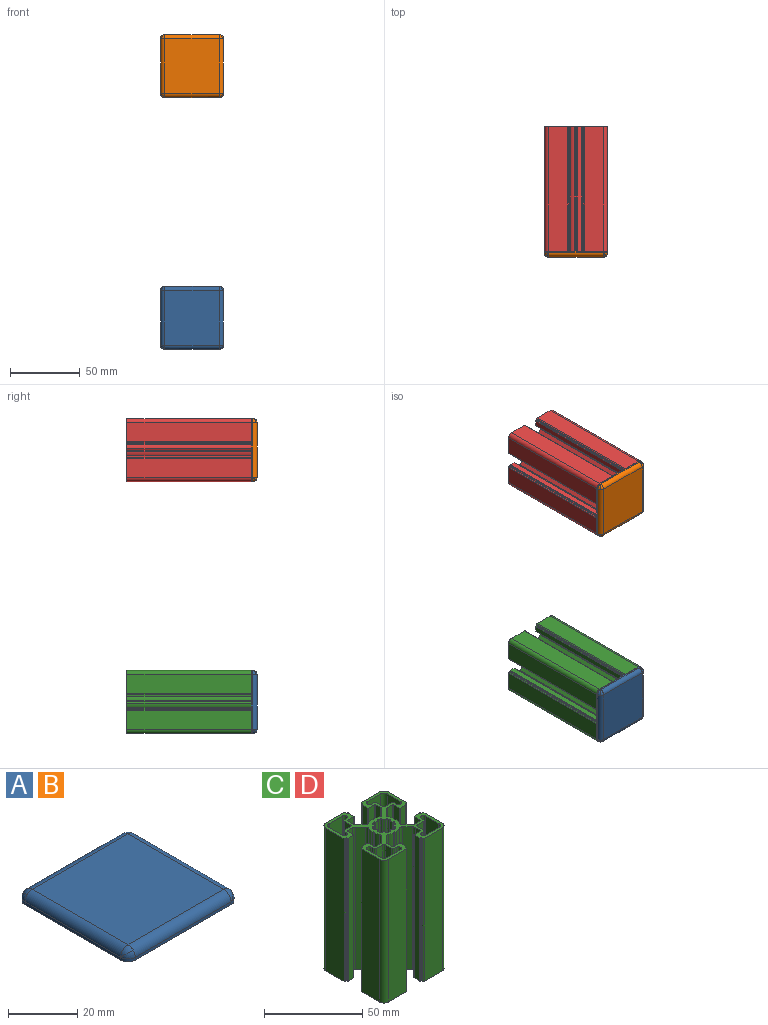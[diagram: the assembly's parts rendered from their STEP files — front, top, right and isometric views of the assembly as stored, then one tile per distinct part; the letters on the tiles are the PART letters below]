
ASSEMBLY  parts=4 mates=3
PART A: 22 faces, bbox 45x45x5.1 mm
  f0: sphere r=3mm, area 7.1mm2, adj f11,f12,f19
  f1: sphere r=3mm, area 7.1mm2, adj f9,f10,f17
  f2: sphere r=3mm, area 7.1mm2, adj f7,f8,f15
  f3: sphere r=3mm, area 7.1mm2, adj f5,f6,f12
  f4: plane 39x39mm, normal (0,0,1), area 1521mm2, adj f6,f8,f10,f12
  f5: sphere r=3mm, area 7.1mm2, adj f3,f12,f13
  f6: cylinder r=3mm len=39mm, axis (-1,0,0), area 183.8mm2, adj f3,f4,f7,f14
  f7: sphere r=3mm, area 7.1mm2, adj f2,f6,f8
  f8: cylinder r=3mm len=39mm, axis (0,-1,0), area 183.8mm2, adj f2,f4,f7,f9,f16
  f9: sphere r=3mm, area 7.1mm2, adj f1,f8,f10
  f10: cylinder r=3mm len=39mm, axis (1,0,0), area 183.8mm2, adj f1,f4,f9,f11,f18
  f11: sphere r=3mm, area 7.1mm2, adj f0,f10,f12
  f12: cylinder r=3mm len=39mm, axis (0,1,0), area 183.8mm2, adj f0,f3,f4,f5,f11,f20
  f13: cylinder r=3mm len=3mm, axis (0,0,-1), area 4.7mm2, adj f5,f14,f20,f21
  f14: plane 39x1mm, normal (0,1,0), area 39mm2, adj f6,f13,f15,f21
  f15: cylinder r=3mm len=3mm, axis (0,0,-1), area 4.7mm2, adj f2,f14,f16,f21
  f16: plane 39x1mm, normal (-1,0,0), area 39mm2, adj f8,f15,f17,f21
  f17: cylinder r=3mm len=3mm, axis (0,0,-1), area 4.7mm2, adj f1,f16,f18,f21
  f18: plane 39x1mm, normal (0,-1,0), area 39mm2, adj f10,f17,f19,f21
  f19: cylinder r=3mm len=3mm, axis (0,0,-1), area 4.7mm2, adj f0,f18,f20,f21
  f20: plane 39x1mm, normal (1,0,0), area 39mm2, adj f12,f13,f19,f21
  f21: plane 45x45mm, normal (0,0,-1), area 2017.3mm2, adj f13,f14,f15,f16,f17,f18,f19,f20
PART B: same geometry as A
PART C: 246 faces, bbox 45x45x89 mm
  f0: cylinder r=1.5mm len=89mm, axis (0,0,1), area 419.4mm2, adj f155,f156,f230,f231
  f1: cylinder r=1.5mm len=89mm, axis (0,0,1), area 419.4mm2, adj f155,f156,f212,f222
  f2: cylinder r=0.5mm len=89mm, axis (0,0,1), area 75.7mm2, adj f155,f156,f187,f188
  f3: cylinder r=0.5mm len=89mm, axis (0,0,1), area 75.7mm2, adj f155,f156,f182,f183
  f4: cylinder r=5mm len=89mm, axis (0,0,1), area 158.9mm2, adj f155,f156,f181,f182
  f5: cylinder r=0.5mm len=89mm, axis (0,0,1), area 75.7mm2, adj f155,f156,f180,f181
  f6: cylinder r=0.5mm len=89mm, axis (0,0,1), area 75.7mm2, adj f155,f156,f175,f176
  f7: cylinder r=0.2mm len=89mm, axis (0,0,1), area 11.2mm2, adj f153,f154,f155,f156
  f8: cylinder r=1.94mm len=89mm, axis (0,0,1), area 216.4mm2, adj f87,f88,f155,f156
  f9: cylinder r=1.94mm len=89mm, axis (0,0,1), area 216.4mm2, adj f79,f80,f155,f156
  f10: cylinder r=0.2mm len=89mm, axis (0,0,1), area 11.2mm2, adj f13,f14,f155,f156
  f11: cylinder r=0.2mm len=89mm, axis (0,0,1), area 4.2mm2, adj f12,f154,f155,f156
  f12: cylinder r=0.2mm len=89mm, axis (0,0,1), area 4.2mm2, adj f11,f13,f155,f156
  f13: plane 89x0.75mm, normal (0.86,0.5,0), area 76.8mm2, adj f10,f12,f155,f156
  f14: cylinder r=8mm len=89mm, axis (0,0,1), area 251.7mm2, adj f10,f15,f155,f156
  f15: cylinder r=1.94mm len=89mm, axis (0,0,1), area 216.4mm2, adj f14,f16,f155,f156
  f16: plane 89x3.57mm, normal (0.71,0.71,0), area 448.9mm2, adj f15,f17,f155,f156
  f17: cylinder r=1.94mm len=89mm, axis (0,0,1), area 135.9mm2, adj f16,f18,f155,f156
  f18: plane 89x3.81mm, normal (0,1,0), area 339.3mm2, adj f17,f19,f155,f156
  f19: cylinder r=0.2mm len=89mm, axis (0,0,1), area 28mm2, adj f18,f20,f155,f156
  f20: plane 89x4.59mm, normal (-1,0,0), area 408.9mm2, adj f19,f21,f155,f156
  f21: cylinder r=0.2mm len=89mm, axis (0,0,1), area 28mm2, adj f20,f22,f155,f156
  f22: plane 89x4mm, normal (0,1,0), area 356.2mm2, adj f21,f23,f155,f156
  f23: cylinder r=0.3mm len=89mm, axis (0,0,1), area 41.9mm2, adj f22,f24,f155,f156
  f24: plane 89x0.2mm, normal (1,0,0), area 17.8mm2, adj f23,f25,f155,f156
  f25: cylinder r=0.3mm len=89mm, axis (0,0,1), area 41.9mm2, adj f24,f26,f155,f156
  f26: plane 89x0.68mm, normal (0,1,0), area 60.6mm2, adj f25,f27,f155,f156
  f27: cylinder r=0.5mm len=89mm, axis (0,0,1), area 69.9mm2, adj f26,f28,f155,f156
  f28: plane 89x13.2mm, normal (1,0,0), area 1174.8mm2, adj f27,f29,f155,f156
  f29: cylinder r=3mm len=89mm, axis (0,0,1), area 419.4mm2, adj f28,f30,f155,f156
  f30: plane 89x13.12mm, normal (0,-1,0), area 1168.1mm2, adj f29,f31,f155,f156
  f31: cylinder r=0.5mm len=89mm, axis (0,0,1), area 69.9mm2, adj f30,f32,f155,f156
  f32: plane 89x0.7mm, normal (-1,0,0), area 62.3mm2, adj f31,f33,f155,f156
  f33: cylinder r=0.3mm len=89mm, axis (0,0,1), area 41.9mm2, adj f32,f34,f155,f156
  f34: plane 89x0.28mm, normal (0,-1,0), area 24.5mm2, adj f33,f35,f155,f156
  f35: cylinder r=0.3mm len=89mm, axis (0,0,1), area 41.9mm2, adj f34,f36,f155,f156
  f36: plane 89x4.03mm, normal (-1,0,0), area 359mm2, adj f35,f37,f155,f156
  f37: cylinder r=0.2mm len=89mm, axis (0,0,1), area 28mm2, adj f36,f38,f155,f156
  f38: plane 89x4.71mm, normal (0,1,0), area 418.8mm2, adj f37,f39,f155,f156
  f39: cylinder r=0.2mm len=89mm, axis (0,0,1), area 28mm2, adj f38,f40,f155,f156
  f40: plane 89x3.8mm, normal (-1,0,0), area 337.8mm2, adj f39,f41,f155,f156
  f41: cylinder r=2mm len=89mm, axis (0,0,1), area 139.8mm2, adj f40,f42,f155,f156
  f42: plane 89x3.57mm, normal (-0.71,-0.71,0), area 449.9mm2, adj f41,f43,f155,f156
  f43: cylinder r=2mm len=89mm, axis (0,0,1), area 218mm2, adj f42,f44,f155,f156
  f44: cylinder r=8.05mm len=89mm, axis (0,0,1), area 260.4mm2, adj f43,f45,f155,f156
  f45: cylinder r=0.2mm len=89mm, axis (0,0,1), area 11.2mm2, adj f44,f46,f155,f156
  f46: plane 89x0.64mm, normal (-0.5,-0.87,0), area 65.9mm2, adj f45,f47,f155,f156
  f47: cylinder r=0.2mm len=89mm, axis (0,0,1), area 12.3mm2, adj f46,f48,f155,f156
  f48: cylinder r=0.2mm len=89mm, axis (0,0,1), area 12.3mm2, adj f47,f49,f155,f156
  f49: plane 89x0.64mm, normal (0.5,-0.87,0), area 65.9mm2, adj f48,f50,f155,f156
  f50: cylinder r=0.2mm len=89mm, axis (0,0,1), area 11.2mm2, adj f49,f51,f155,f156
  f51: cylinder r=8.05mm len=89mm, axis (0,0,1), area 260.4mm2, adj f50,f52,f155,f156
  f52: cylinder r=2mm len=89mm, axis (0,0,1), area 218mm2, adj f51,f53,f155,f156
  f53: plane 89x3.57mm, normal (0.71,-0.71,0), area 449.9mm2, adj f52,f54,f155,f156
  f54: cylinder r=2mm len=89mm, axis (0,0,1), area 139.8mm2, adj f53,f55,f155,f156
  f55: plane 89x3.8mm, normal (1,0,0), area 337.8mm2, adj f54,f56,f155,f156
  f56: cylinder r=0.2mm len=89mm, axis (0,0,1), area 28mm2, adj f55,f57,f155,f156
  f57: plane 89x4.71mm, normal (0,1,0), area 418.8mm2, adj f56,f58,f155,f156
  f58: cylinder r=0.2mm len=89mm, axis (0,0,1), area 28mm2, adj f57,f59,f155,f156
  f59: plane 89x4.03mm, normal (1,0,0), area 359mm2, adj f58,f60,f155,f156
  f60: cylinder r=0.3mm len=89mm, axis (0,0,1), area 41.9mm2, adj f59,f61,f155,f156
  f61: plane 89x0.28mm, normal (0,-1,0), area 24.5mm2, adj f60,f62,f155,f156
  f62: cylinder r=0.3mm len=89mm, axis (0,0,1), area 41.9mm2, adj f61,f63,f155,f156
  f63: plane 89x0.7mm, normal (1,0,0), area 62.3mm2, adj f62,f64,f155,f156
  f64: cylinder r=0.5mm len=89mm, axis (0,0,1), area 69.9mm2, adj f63,f65,f155,f156
  f65: plane 89x13.12mm, normal (0,-1,0), area 1168.1mm2, adj f64,f66,f155,f156
  f66: cylinder r=3mm len=89mm, axis (0,0,1), area 419.4mm2, adj f65,f67,f155,f156
  f67: plane 89x13.2mm, normal (-1,0,0), area 1174.8mm2, adj f66,f68,f155,f156
  f68: cylinder r=0.5mm len=89mm, axis (0,0,1), area 69.9mm2, adj f67,f69,f155,f156
  f69: plane 89x0.68mm, normal (0,1,0), area 60.6mm2, adj f68,f70,f155,f156
  f70: cylinder r=0.3mm len=89mm, axis (0,0,1), area 41.9mm2, adj f69,f71,f155,f156
  f71: plane 89x0.2mm, normal (-1,0,0), area 17.8mm2, adj f70,f72,f155,f156
  f72: cylinder r=0.3mm len=89mm, axis (0,0,1), area 41.9mm2, adj f71,f73,f155,f156
  f73: plane 89x4mm, normal (0,1,0), area 356.2mm2, adj f72,f74,f155,f156
  f74: cylinder r=0.2mm len=89mm, axis (0,0,1), area 28mm2, adj f73,f75,f155,f156
  f75: plane 89x4.59mm, normal (1,0,0), area 408.9mm2, adj f74,f76,f155,f156
  f76: cylinder r=0.2mm len=89mm, axis (0,0,1), area 28mm2, adj f75,f77,f155,f156
  f77: plane 89x3.81mm, normal (0,1,0), area 339.3mm2, adj f76,f78,f155,f156
  f78: cylinder r=1.94mm len=89mm, axis (0,0,1), area 135.9mm2, adj f77,f79,f155,f156
  f79: plane 89x3.57mm, normal (-0.71,0.71,0), area 448.9mm2, adj f9,f78,f155,f156
  f80: cylinder r=8mm len=89mm, axis (0,0,1), area 251.7mm2, adj f9,f81,f155,f156
  f81: cylinder r=0.2mm len=89mm, axis (0,0,1), area 11.2mm2, adj f80,f82,f155,f156
  f82: plane 89x0.75mm, normal (-0.86,0.5,0), area 76.8mm2, adj f81,f83,f155,f156
  f83: cylinder r=0.2mm len=89mm, axis (0,0,1), area 4.2mm2, adj f82,f84,f155,f156
  f84: cylinder r=0.2mm len=89mm, axis (0,0,1), area 4.2mm2, adj f83,f85,f155,f156
  f85: plane 89x0.75mm, normal (-0.86,-0.5,0), area 76.8mm2, adj f84,f86,f155,f156
  f86: cylinder r=0.2mm len=89mm, axis (0,0,1), area 11.2mm2, adj f85,f87,f155,f156
  f87: cylinder r=8mm len=89mm, axis (0,0,1), area 251.7mm2, adj f8,f86,f155,f156
  f88: plane 89x3.57mm, normal (-0.71,-0.71,0), area 448.9mm2, adj f8,f89,f155,f156
  f89: cylinder r=1.94mm len=89mm, axis (0,0,1), area 135.9mm2, adj f88,f90,f155,f156
  f90: plane 89x3.81mm, normal (0,-1,0), area 339.3mm2, adj f89,f91,f155,f156
  f91: cylinder r=0.2mm len=89mm, axis (0,0,1), area 28mm2, adj f90,f92,f155,f156
  f92: plane 89x4.59mm, normal (1,0,0), area 408.9mm2, adj f91,f93,f155,f156
  f93: cylinder r=0.2mm len=89mm, axis (0,0,1), area 28mm2, adj f92,f94,f155,f156
  f94: plane 89x4mm, normal (0,-1,0), area 356.2mm2, adj f93,f95,f155,f156
  f95: cylinder r=0.3mm len=89mm, axis (0,0,1), area 41.9mm2, adj f94,f96,f155,f156
  f96: plane 89x0.2mm, normal (-1,0,0), area 17.8mm2, adj f95,f97,f155,f156
  f97: cylinder r=0.3mm len=89mm, axis (0,0,1), area 41.9mm2, adj f96,f98,f155,f156
  f98: plane 89x0.68mm, normal (0,-1,0), area 60.6mm2, adj f97,f99,f155,f156
  f99: cylinder r=0.5mm len=89mm, axis (0,0,1), area 69.9mm2, adj f98,f100,f155,f156
  f100: plane 89x13.2mm, normal (-1,0,0), area 1174.8mm2, adj f99,f101,f155,f156
  f101: cylinder r=3mm len=89mm, axis (0,0,1), area 419.4mm2, adj f100,f102,f155,f156
  f102: plane 89x13.12mm, normal (0,1,0), area 1168.1mm2, adj f101,f103,f155,f156
  f103: cylinder r=0.5mm len=89mm, axis (0,0,1), area 69.9mm2, adj f102,f104,f155,f156
  f104: plane 89x0.7mm, normal (1,0,0), area 62.3mm2, adj f103,f105,f155,f156
  f105: cylinder r=0.3mm len=89mm, axis (0,0,1), area 41.9mm2, adj f104,f106,f155,f156
  f106: plane 89x0.28mm, normal (0,1,0), area 24.5mm2, adj f105,f107,f155,f156
  f107: cylinder r=0.3mm len=89mm, axis (0,0,1), area 41.9mm2, adj f106,f108,f155,f156
  f108: plane 89x4.03mm, normal (1,0,0), area 359mm2, adj f107,f109,f155,f156
  f109: cylinder r=0.2mm len=89mm, axis (0,0,1), area 28mm2, adj f108,f110,f155,f156
  f110: plane 89x4.71mm, normal (0,-1,0), area 418.8mm2, adj f109,f111,f155,f156
  f111: cylinder r=0.2mm len=89mm, axis (0,0,1), area 28mm2, adj f110,f112,f155,f156
  f112: plane 89x3.8mm, normal (1,0,0), area 337.8mm2, adj f111,f113,f155,f156
  f113: cylinder r=2mm len=89mm, axis (0,0,1), area 139.8mm2, adj f112,f114,f155,f156
  f114: plane 89x3.57mm, normal (0.71,0.71,0), area 449.9mm2, adj f113,f115,f155,f156
  f115: cylinder r=2mm len=89mm, axis (0,0,1), area 218mm2, adj f114,f116,f155,f156
  f116: cylinder r=8.05mm len=89mm, axis (0,0,1), area 260.4mm2, adj f115,f117,f155,f156
  f117: cylinder r=0.2mm len=89mm, axis (0,0,1), area 11.2mm2, adj f116,f118,f155,f156
  f118: plane 89x0.64mm, normal (0.5,0.87,0), area 65.9mm2, adj f117,f119,f155,f156
  f119: cylinder r=0.2mm len=89mm, axis (0,0,1), area 12.3mm2, adj f118,f120,f155,f156
  f120: cylinder r=0.2mm len=89mm, axis (0,0,1), area 12.3mm2, adj f119,f121,f155,f156
  f121: plane 89x0.64mm, normal (-0.5,0.87,0), area 65.9mm2, adj f120,f122,f155,f156
  f122: cylinder r=0.2mm len=89mm, axis (0,0,1), area 11.2mm2, adj f121,f123,f155,f156
  f123: cylinder r=8.05mm len=89mm, axis (0,0,1), area 260.4mm2, adj f122,f124,f155,f156
  f124: cylinder r=2mm len=89mm, axis (0,0,1), area 218mm2, adj f123,f125,f155,f156
  f125: plane 89x3.57mm, normal (-0.71,0.71,0), area 449.9mm2, adj f124,f126,f155,f156
  f126: cylinder r=2mm len=89mm, axis (0,0,1), area 139.8mm2, adj f125,f127,f155,f156
  f127: plane 89x3.8mm, normal (-1,0,0), area 337.8mm2, adj f126,f128,f155,f156
  f128: cylinder r=0.2mm len=89mm, axis (0,0,1), area 28mm2, adj f127,f129,f155,f156
  f129: plane 89x4.71mm, normal (0,-1,0), area 418.8mm2, adj f128,f130,f155,f156
  f130: cylinder r=0.2mm len=89mm, axis (0,0,1), area 28mm2, adj f129,f131,f155,f156
  f131: plane 89x4.03mm, normal (-1,0,0), area 359mm2, adj f130,f132,f155,f156
  f132: cylinder r=0.3mm len=89mm, axis (0,0,1), area 41.9mm2, adj f131,f133,f155,f156
  f133: plane 89x0.28mm, normal (0,1,0), area 24.5mm2, adj f132,f134,f155,f156
  f134: cylinder r=0.3mm len=89mm, axis (0,0,1), area 41.9mm2, adj f133,f135,f155,f156
  f135: plane 89x0.7mm, normal (-1,0,0), area 62.3mm2, adj f134,f136,f155,f156
  f136: cylinder r=0.5mm len=89mm, axis (0,0,1), area 69.9mm2, adj f135,f137,f155,f156
  f137: plane 89x13.12mm, normal (0,1,0), area 1168.1mm2, adj f136,f138,f155,f156
  f138: cylinder r=3mm len=89mm, axis (0,0,1), area 419.4mm2, adj f137,f139,f155,f156
  f139: plane 89x13.2mm, normal (1,0,0), area 1174.8mm2, adj f138,f140,f155,f156
  f140: cylinder r=0.5mm len=89mm, axis (0,0,1), area 69.9mm2, adj f139,f141,f155,f156
  f141: plane 89x0.68mm, normal (0,-1,0), area 60.6mm2, adj f140,f142,f155,f156
  f142: cylinder r=0.3mm len=89mm, axis (0,0,1), area 41.9mm2, adj f141,f143,f155,f156
  f143: plane 89x0.2mm, normal (1,0,0), area 17.8mm2, adj f142,f144,f155,f156
  f144: cylinder r=0.3mm len=89mm, axis (0,0,1), area 41.9mm2, adj f143,f145,f155,f156
  f145: plane 89x4mm, normal (0,-1,0), area 356.2mm2, adj f144,f146,f155,f156
  f146: cylinder r=0.2mm len=89mm, axis (0,0,1), area 28mm2, adj f145,f147,f155,f156
  f147: plane 89x4.59mm, normal (-1,0,0), area 408.9mm2, adj f146,f148,f155,f156
  f148: cylinder r=0.2mm len=89mm, axis (0,0,1), area 28mm2, adj f147,f149,f155,f156
  f149: plane 89x3.81mm, normal (0,-1,0), area 339.3mm2, adj f148,f150,f155,f156
  f150: cylinder r=1.94mm len=89mm, axis (0,0,1), area 135.9mm2, adj f149,f151,f155,f156
  f151: plane 89x3.57mm, normal (0.71,-0.71,0), area 448.9mm2, adj f150,f152,f155,f156
  f152: cylinder r=1.94mm len=89mm, axis (0,0,1), area 216.4mm2, adj f151,f153,f155,f156
  f153: cylinder r=8mm len=89mm, axis (0,0,1), area 251.7mm2, adj f7,f152,f155,f156
  f154: plane 89x0.75mm, normal (0.86,-0.5,0), area 76.8mm2, adj f7,f11,f155,f156
  f155: plane 45x45mm, normal (0,0,-1), area 571.4mm2, adj f0,f1,f2,f3,f4,f5,f6,f7
  f156: plane 45x45mm, normal (0,0,1), area 571.4mm2, adj f0,f1,f2,f3,f4,f5,f6,f7
  f157: cylinder r=1.5mm len=89mm, axis (0,0,1), area 419.4mm2, adj f155,f156,f158,f168
  f158: plane 89x9.5mm, normal (0,-1,0), area 845.5mm2, adj f155,f156,f157,f159
  f159: cylinder r=2.5mm len=89mm, axis (0,0,1), area 349.5mm2, adj f155,f156,f158,f160
  f160: plane 89x9.5mm, normal (-1,0,0), area 845.5mm2, adj f155,f156,f159,f161
  f161: cylinder r=1.5mm len=89mm, axis (0,0,1), area 419.4mm2, adj f155,f156,f160,f162
  f162: plane 89x1.55mm, normal (1,0,0), area 137.9mm2, adj f155,f156,f161,f163
  f163: cylinder r=1mm len=89mm, axis (0,0,1), area 139.8mm2, adj f155,f156,f162,f164
  f164: plane 89x4.45mm, normal (0,1,0), area 396.1mm2, adj f155,f156,f163,f165
  f165: cylinder r=1mm len=89mm, axis (0,0,1), area 139.8mm2, adj f155,f156,f164,f166
  f166: plane 89x4.45mm, normal (1,0,0), area 396.1mm2, adj f155,f156,f165,f167
  f167: cylinder r=1mm len=89mm, axis (0,0,1), area 139.8mm2, adj f155,f156,f166,f168
  f168: plane 89x1.55mm, normal (0,1,0), area 137.9mm2, adj f155,f156,f157,f167
  f169: cylinder r=6.1mm len=89mm, axis (0,0,1), area 139.8mm2, adj f155,f156,f170,f211
  f170: cylinder r=0.5mm len=89mm, axis (0,0,1), area 75.6mm2, adj f155,f156,f169,f171
  f171: plane 89x0.56mm, normal (-0.98,-0.18,0), area 50.4mm2, adj f155,f156,f170,f172
  f172: cylinder r=5mm len=89mm, axis (0,0,1), area 155.2mm2, adj f155,f156,f171,f173
  f173: plane 89x0.56mm, normal (0.98,-0.18,0), area 50.4mm2, adj f155,f156,f172,f174
  f174: cylinder r=0.5mm len=89mm, axis (0,0,1), area 75.6mm2, adj f155,f156,f173,f175
  f175: cylinder r=6.1mm len=89mm, axis (0,0,1), area 139.8mm2, adj f6,f155,f156,f174
  f176: plane 89x0.46mm, normal (-0.82,0.58,0), area 50.5mm2, adj f6,f155,f156,f177
  f177: cylinder r=5mm len=89mm, axis (0,0,1), area 154.8mm2, adj f155,f156,f176,f178
  f178: plane 89x0.48mm, normal (0.57,-0.82,0), area 51.7mm2, adj f155,f156,f177,f179
  f179: cylinder r=0.5mm len=89mm, axis (0,0,1), area 75.6mm2, adj f155,f156,f178,f180
  f180: cylinder r=6.1mm len=89mm, axis (0,0,1), area 139.8mm2, adj f5,f155,f156,f179
  f181: plane 89x0.57mm, normal (-0.17,0.99,0), area 51.4mm2, adj f4,f5,f155,f156
  f182: plane 89x0.57mm, normal (-0.17,-0.99,0), area 51.4mm2, adj f3,f4,f155,f156
  f183: cylinder r=6.1mm len=89mm, axis (0,0,1), area 139.8mm2, adj f3,f155,f156,f184
  f184: cylinder r=0.5mm len=89mm, axis (0,0,1), area 75.6mm2, adj f155,f156,f183,f185
  f185: plane 89x0.48mm, normal (0.57,0.82,0), area 51.7mm2, adj f155,f156,f184,f186
  f186: cylinder r=5mm len=89mm, axis (0,0,1), area 154.8mm2, adj f155,f156,f185,f187
  f187: plane 89x0.46mm, normal (-0.82,-0.58,0), area 50.5mm2, adj f2,f155,f156,f186
  f188: cylinder r=6.1mm len=89mm, axis (0,0,1), area 139.8mm2, adj f2,f155,f156,f189
  f189: cylinder r=0.5mm len=89mm, axis (0,0,1), area 75.6mm2, adj f155,f156,f188,f190
  f190: plane 89x0.56mm, normal (0.98,0.18,0), area 50.4mm2, adj f155,f156,f189,f191
  f191: cylinder r=5mm len=89mm, axis (0,0,1), area 155.2mm2, adj f155,f156,f190,f192
  f192: plane 89x0.56mm, normal (-0.98,0.18,0), area 50.4mm2, adj f155,f156,f191,f193
  f193: cylinder r=0.5mm len=89mm, axis (0,0,1), area 75.6mm2, adj f155,f156,f192,f194
  f194: cylinder r=6.1mm len=89mm, axis (0,0,1), area 139.8mm2, adj f155,f156,f193,f195
  f195: cylinder r=0.5mm len=89mm, axis (0,0,1), area 75.7mm2, adj f155,f156,f194,f196
  f196: plane 89x0.46mm, normal (0.82,-0.58,0), area 50.5mm2, adj f155,f156,f195,f197
  f197: cylinder r=5mm len=89mm, axis (0,0,1), area 154.8mm2, adj f155,f156,f196,f198
  f198: plane 89x0.48mm, normal (-0.57,0.82,0), area 51.7mm2, adj f155,f156,f197,f199
  f199: cylinder r=0.5mm len=89mm, axis (0,0,1), area 75.6mm2, adj f155,f156,f198,f200
  f200: cylinder r=6.1mm len=89mm, axis (0,0,1), area 139.8mm2, adj f155,f156,f199,f201
  f201: cylinder r=0.5mm len=89mm, axis (0,0,1), area 75.7mm2, adj f155,f156,f200,f202
  f202: plane 89x0.57mm, normal (0.17,-0.99,0), area 51.4mm2, adj f155,f156,f201,f203
  f203: cylinder r=5mm len=89mm, axis (0,0,1), area 158.9mm2, adj f155,f156,f202,f204
  f204: plane 89x0.57mm, normal (0.17,0.99,0), area 51.4mm2, adj f155,f156,f203,f205
  f205: cylinder r=0.5mm len=89mm, axis (0,0,1), area 75.7mm2, adj f155,f156,f204,f206
  f206: cylinder r=6.1mm len=89mm, axis (0,0,1), area 139.8mm2, adj f155,f156,f205,f207
  f207: cylinder r=0.5mm len=89mm, axis (0,0,1), area 75.6mm2, adj f155,f156,f206,f208
  f208: plane 89x0.48mm, normal (-0.57,-0.82,0), area 51.7mm2, adj f155,f156,f207,f209
  f209: cylinder r=5mm len=89mm, axis (0,0,1), area 154.8mm2, adj f155,f156,f208,f210
  f210: plane 89x0.46mm, normal (0.82,0.58,0), area 50.5mm2, adj f155,f156,f209,f211
  f211: cylinder r=0.5mm len=89mm, axis (0,0,1), area 75.7mm2, adj f155,f156,f169,f210
  f212: plane 89x9.5mm, normal (0,1,0), area 845.5mm2, adj f1,f155,f156,f213
  f213: cylinder r=2.5mm len=89mm, axis (0,0,1), area 349.5mm2, adj f155,f156,f212,f214
  f214: plane 89x9.5mm, normal (1,0,0), area 845.5mm2, adj f155,f156,f213,f215
  f215: cylinder r=1.5mm len=89mm, axis (0,0,1), area 419.4mm2, adj f155,f156,f214,f216
  f216: plane 89x1.55mm, normal (-1,0,0), area 137.9mm2, adj f155,f156,f215,f217
  f217: cylinder r=1mm len=89mm, axis (0,0,1), area 139.8mm2, adj f155,f156,f216,f218
  f218: plane 89x4.45mm, normal (0,-1,0), area 396.1mm2, adj f155,f156,f217,f219
  f219: cylinder r=1mm len=89mm, axis (0,0,1), area 139.8mm2, adj f155,f156,f218,f220
  f220: plane 89x4.45mm, normal (-1,0,0), area 396.1mm2, adj f155,f156,f219,f221
  f221: cylinder r=1mm len=89mm, axis (0,0,1), area 139.8mm2, adj f155,f156,f220,f222
  f222: plane 89x1.55mm, normal (0,-1,0), area 137.9mm2, adj f1,f155,f156,f221
  f223: cylinder r=1mm len=89mm, axis (0,0,1), area 139.8mm2, adj f155,f156,f224,f233
  f224: plane 89x4.45mm, normal (0,1,0), area 396.1mm2, adj f155,f156,f223,f225
  f225: cylinder r=1mm len=89mm, axis (0,0,1), area 139.8mm2, adj f155,f156,f224,f226
  f226: plane 89x1.55mm, normal (-1,0,0), area 137.9mm2, adj f155,f156,f225,f227
  f227: cylinder r=1.5mm len=89mm, axis (0,0,1), area 419.4mm2, adj f155,f156,f226,f228
  f228: plane 89x9.5mm, normal (1,0,0), area 845.5mm2, adj f155,f156,f227,f229
  f229: cylinder r=2.5mm len=89mm, axis (0,0,1), area 349.5mm2, adj f155,f156,f228,f230
  f230: plane 89x9.5mm, normal (0,-1,0), area 845.5mm2, adj f0,f155,f156,f229
  f231: plane 89x1.55mm, normal (0,1,0), area 137.9mm2, adj f0,f155,f156,f232
  f232: cylinder r=1mm len=89mm, axis (0,0,1), area 139.8mm2, adj f155,f156,f231,f233
  f233: plane 89x4.45mm, normal (-1,0,0), area 396.1mm2, adj f155,f156,f223,f232
  f234: cylinder r=1mm len=89mm, axis (0,0,1), area 139.8mm2, adj f155,f156,f235,f245
  f235: plane 89x4.45mm, normal (1,0,0), area 396.1mm2, adj f155,f156,f234,f236
  f236: cylinder r=1mm len=89mm, axis (0,0,1), area 139.8mm2, adj f155,f156,f235,f237
  f237: plane 89x4.45mm, normal (0,-1,0), area 396.1mm2, adj f155,f156,f236,f238
  f238: cylinder r=1mm len=89mm, axis (0,0,1), area 139.8mm2, adj f155,f156,f237,f239
  f239: plane 89x1.55mm, normal (1,0,0), area 137.9mm2, adj f155,f156,f238,f240
  f240: cylinder r=1.5mm len=89mm, axis (0,0,1), area 419.4mm2, adj f155,f156,f239,f241
  f241: plane 89x9.5mm, normal (-1,0,0), area 845.5mm2, adj f155,f156,f240,f242
  f242: cylinder r=2.5mm len=89mm, axis (0,0,1), area 349.5mm2, adj f155,f156,f241,f243
  f243: plane 89x9.5mm, normal (0,1,0), area 845.5mm2, adj f155,f156,f242,f244
  f244: cylinder r=1.5mm len=89mm, axis (0,0,1), area 419.4mm2, adj f155,f156,f243,f245
  f245: plane 89x1.55mm, normal (0,-1,0), area 137.9mm2, adj f155,f156,f234,f244
PART D: same geometry as C
PLACE A rot(axis=(1,0,0),90deg) t=(-2062.91,940.98,-660.12)mm
PLACE B rot(axis=(1,0,0),90deg) t=(-2062.91,940.98,-480.12)mm
PLACE C rot(axis=(1,0,0),90deg) t=(-2062.91,940.98,-660.12)mm
PLACE D rot(axis=(1,0,0),90deg) t=(-2062.91,940.98,-480.12)mm
MATE fastened B.f21 <-> D.f4  axis (0,1,0) through (-2062.91,940.98,-480.12)mm
MATE fastened A.f21 <-> C.f4  axis (0,1,0) through (-2062.91,940.98,-660.12)mm
MATE fastened C.f155 <-> D.f155  axis (0,1,0) through (-2043.41,1029.98,-637.62)mm
